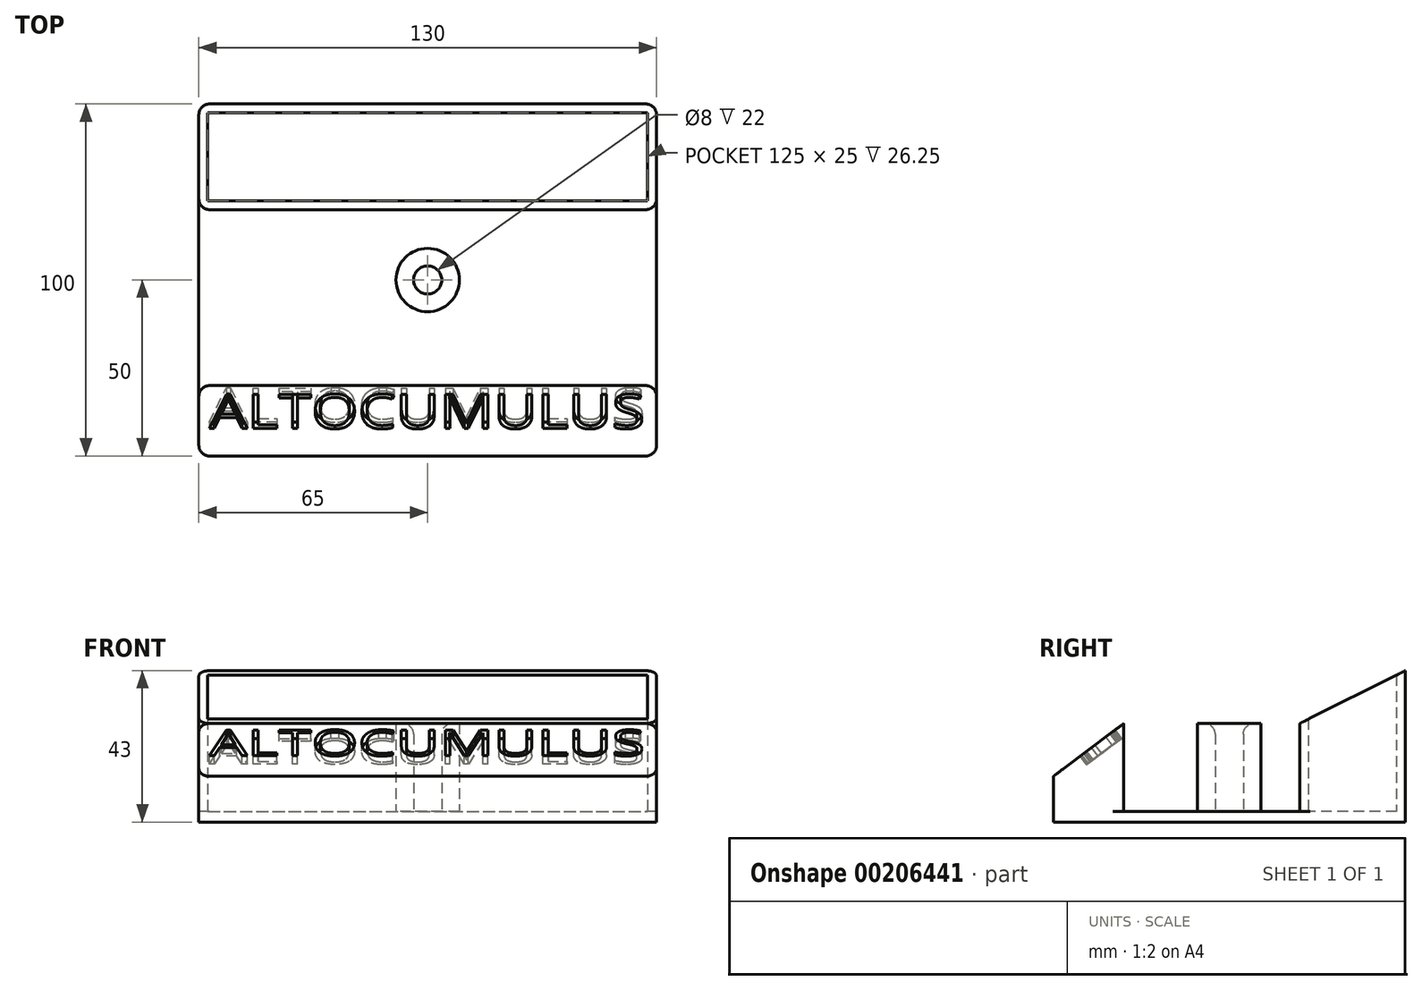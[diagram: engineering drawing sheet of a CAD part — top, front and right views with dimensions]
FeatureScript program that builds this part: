
annotation { "Feature Type Name" : "Feature", "Feature Type Description" : "" }
export const myFeature = defineFeature(function(context is Context, id is Id, definition is map)
    precondition{}
    {
        {
            var Q0;
            Q0=qCreatedBy(makeId("Top.planeOp"),FACE);
            var sketch = newSketch(context, id + "F0", { "sketchPlane" : qUnion([Q0])});
            skLineSegment(sketch, "E0.bottom", {"start": v(-65, 100) * mm, "end": v(65, 100) * mm});
            skLineSegment(sketch, "E0.top", {"start": v(-65, 0) * mm, "end": v(65, 0) * mm});
            skLineSegment(sketch, "E0.left", {"start": v(65, 100) * mm, "end": v(65, 0) * mm});
            skLineSegment(sketch, "E0.right", {"start": v(-65, 100) * mm, "end": v(-65, 0) * mm});
            skSolve(sketch);
        }
        {
            var Q0;
            Q0=makeQuery(id+"F0.imprint","IMPRINT",FACE,{"disambiguationData":[TD([[makeQuery(id+"F0.imprint","IMPRINT",EDGE,{"derivedFrom":sQuery(id+"F0.wireOp",EDGE,"E0.bottom")}),-1.0]])]});
            extrude(context, id + "F1", {"entities" : qUnion([Q0]), "depth" : 3 * mm});
        }
        {
            var Q0;
            Q0=makeQuery(id+"F1.opExtrude","CAP_FACE",FACE,{"disambiguationData":[OSD([sQuery(id+"F0.wireOp",EDGE,"E0.bottom"),sQuery(id+"F0.wireOp",EDGE,"E0.top"),sQuery(id+"F0.wireOp",EDGE,"E0.left"),sQuery(id+"F0.wireOp",EDGE,"E0.right")])],"isStart":false});
            var sketch = newSketch(context, id + "F2", { "sketchPlane" : qUnion([Q0])});
            skLineSegment(sketch, "E1", {"start": v(0, 0) * mm, "end": v(0, 100) * mm, "construction": true});
            skCircle(sketch, "E2", {"center": v(0, 50) * mm, "radius": 9 * mm});
            skCircle(sketch, "E3", {"center": v(0, 50) * mm, "radius": 4 * mm});
            skLineSegment(sketch, "E4.bottom", {"start": v(-65, 0) * mm, "end": v(65, 0) * mm});
            skLineSegment(sketch, "E4.top", {"start": v(-65, 20) * mm, "end": v(65, 20) * mm});
            skLineSegment(sketch, "E4.left", {"start": v(-65, 0) * mm, "end": v(-65, 20) * mm});
            skLineSegment(sketch, "E4.right", {"start": v(65, 0) * mm, "end": v(65, 20) * mm});
            skLineSegment(sketch, "E5.bottom", {"start": v(-65, 100) * mm, "end": v(65, 100) * mm});
            skLineSegment(sketch, "E5.top", {"start": v(-65, 70) * mm, "end": v(65, 70) * mm});
            skLineSegment(sketch, "E5.left", {"start": v(-65, 100) * mm, "end": v(-65, 70) * mm});
            skLineSegment(sketch, "E5.right", {"start": v(65, 100) * mm, "end": v(65, 70) * mm});
            skLineSegment(sketch, "E6.0", {"start": v(62.5, 97.5) * mm, "end": v(62.5, 72.5) * mm});
            skLineSegment(sketch, "E6.1", {"start": v(-62.5, 97.5) * mm, "end": v(62.5, 97.5) * mm});
            skLineSegment(sketch, "E6.2", {"start": v(-62.5, 97.5) * mm, "end": v(-62.5, 72.5) * mm});
            skLineSegment(sketch, "E6.3", {"start": v(-62.5, 72.5) * mm, "end": v(62.5, 72.5) * mm});
            skSolve(sketch);
        }
        {
            var Q0;
            Q0=makeQuery(id+"F2.imprint","IMPRINT",FACE,{"disambiguationData":[TD([[makeQuery(id+"F2.imprint","IMPRINT",EDGE,{"derivedFrom":sQuery(id+"F2.wireOp",EDGE,"E5.bottom")}),-1.0]])]});
            extrude(context, id + "F3", {"entities" : qUnion([Q0]), "operationType" : NewBodyOperationType.ADD, "depth" : 40 * mm});
        }
        {
            var Q0;
            Q0=makeQuery(id+"F2.imprint","IMPRINT",FACE,{"disambiguationData":[TD([[makeQuery(id+"F2.imprint","IMPRINT",EDGE,{"derivedFrom":sQuery(id+"F2.wireOp",EDGE,"E2")}),1.0]])]});
            var Q1;
            Q1=makeQuery(id+"F2.imprint","IMPRINT",FACE,{"disambiguationData":[TD([[makeQuery(id+"F2.imprint","IMPRINT",EDGE,{"derivedFrom":sQuery(id+"F2.wireOp",EDGE,"E4.bottom")}),1.0]])]});
            extrude(context, id + "F4", {"entities" : qUnion([Q0, Q1]), "operationType" : NewBodyOperationType.ADD, "depth" : 25 * mm});
        }
        {
            var Q0;
            Q0=makeQuery(id+"F4.opExtrude","CAP_EDGE",EDGE,{"disambiguationData":[OSD([sQuery(id+"F2.wireOp",EDGE,"E4.bottom")])],"isStart":false});
            chamfer(context, id + "F5", {"entities" : qUnion([Q0]), "chamferType" : ChamferType.TWO_OFFSETS, "width1" : 20 * mm, "oppositeDirection" : false, "width2" : 15 * mm, "tangentPropagation" : true});
        }
        {
            var Q0;
            Q0=makeQuery(id+"F3.opExtrude","CAP_EDGE",EDGE,{"disambiguationData":[OSD([sQuery(id+"F2.wireOp",EDGE,"E5.top")])],"isStart":false});
            chamfer(context, id + "F6", {"entities" : qUnion([Q0]), "chamferType" : ChamferType.TWO_OFFSETS, "width1" : 30 * mm, "oppositeDirection" : false, "width2" : 15 * mm, "tangentPropagation" : true});
        }
        {
            var Q0;
            Q0=makeQuery(id+"F3.boolean.opBoolean","MERGE",EDGE,{"derivedFrom":[makeQuery(id+"F1.opExtrude","SWEPT_EDGE",EDGE,{"disambiguationData":[OSD([sQuery(id+"F0.wireOp",EDGE,"E0.bottom"),sQuery(id+"F0.wireOp",EDGE,"E0.right")])]}),makeQuery(id+"F3.opExtrude","SWEPT_EDGE",EDGE,{"disambiguationData":[OSD([sQuery(id+"F2.wireOp",EDGE,"E5.bottom"),sQuery(id+"F2.wireOp",EDGE,"E5.left")])]})]});
            var Q1;
            Q1=makeQuery(id+"F3.opExtrude","SWEPT_EDGE",EDGE,{"disambiguationData":[OSD([sQuery(id+"F0.wireOp",EDGE,"E0.right"),sQuery(id+"F2.wireOp",EDGE,"E5.top"),sQuery(id+"F2.wireOp",EDGE,"E5.left")])]});
            var Q2;
            Q2=makeQuery(id+"F3.opExtrude","SWEPT_EDGE",EDGE,{"disambiguationData":[OSD([sQuery(id+"F0.wireOp",EDGE,"E0.left"),sQuery(id+"F2.wireOp",EDGE,"E5.top"),sQuery(id+"F2.wireOp",EDGE,"E5.right")])]});
            var Q3;
            Q3=makeQuery(id+"F4.boolean.opBoolean","MERGE",EDGE,{"derivedFrom":[makeQuery(id+"F1.opExtrude","SWEPT_EDGE",EDGE,{"disambiguationData":[OSD([sQuery(id+"F0.wireOp",EDGE,"E0.top"),sQuery(id+"F0.wireOp",EDGE,"E0.right")])]}),makeQuery(id+"F4.opExtrude","SWEPT_EDGE",EDGE,{"disambiguationData":[OSD([sQuery(id+"F2.wireOp",EDGE,"E4.bottom"),sQuery(id+"F2.wireOp",EDGE,"E4.left")])]})]});
            var Q4;
            Q4=makeQuery(id+"F3.boolean.opBoolean","MERGE",EDGE,{"derivedFrom":[makeQuery(id+"F1.opExtrude","SWEPT_EDGE",EDGE,{"disambiguationData":[OSD([sQuery(id+"F0.wireOp",EDGE,"E0.bottom"),sQuery(id+"F0.wireOp",EDGE,"E0.left")])]}),makeQuery(id+"F3.opExtrude","SWEPT_EDGE",EDGE,{"disambiguationData":[OSD([sQuery(id+"F2.wireOp",EDGE,"E5.bottom"),sQuery(id+"F2.wireOp",EDGE,"E5.right")])]})]});
            var Q5;
            Q5=makeQuery(id+"F4.boolean.opBoolean","MERGE",EDGE,{"derivedFrom":[makeQuery(id+"F1.opExtrude","SWEPT_EDGE",EDGE,{"disambiguationData":[OSD([sQuery(id+"F0.wireOp",EDGE,"E0.top"),sQuery(id+"F0.wireOp",EDGE,"E0.left")])]}),makeQuery(id+"F4.opExtrude","SWEPT_EDGE",EDGE,{"disambiguationData":[OSD([sQuery(id+"F2.wireOp",EDGE,"E4.bottom"),sQuery(id+"F2.wireOp",EDGE,"E4.right")])]})]});
            var Q6;
            Q6=makeQuery(id+"F4.opExtrude","SWEPT_EDGE",EDGE,{"disambiguationData":[OSD([sQuery(id+"F0.wireOp",EDGE,"E0.left"),sQuery(id+"F2.wireOp",EDGE,"E4.top"),sQuery(id+"F2.wireOp",EDGE,"E4.right")])]});
            var Q7;
            Q7=makeQuery(id+"F4.opExtrude","SWEPT_EDGE",EDGE,{"disambiguationData":[OSD([sQuery(id+"F0.wireOp",EDGE,"E0.right"),sQuery(id+"F2.wireOp",EDGE,"E4.top"),sQuery(id+"F2.wireOp",EDGE,"E4.left")])]});
            var Q8;
            Q8=makeQuery(id+"F4.opExtrude","CAP_EDGE",EDGE,{"disambiguationData":[OSD([sQuery(id+"F2.wireOp",EDGE,"E3")])],"isStart":false});
            fillet(context, id + "F7", {"entities" : qUnion([Q0, Q1, Q2, Q3, Q4, Q5, Q6, Q7, Q8]), "radius" : 3 * mm, "tangentPropagation" : true, "allowEdgeOverflow" : false});
        }
        {
            var Q0;
            Q0=makeQuery(id+"F5.opChamfer","BLEND_FACE",FACE,{"disambiguationData":[OSD([sQuery(id+"F2.wireOp",EDGE,"E4.bottom")])]});
            var sketch = newSketch(context, id + "F8", { "sketchPlane" : qUnion([Q0])});
            skLineSegment(sketch, "E7.0", {"start": v(62, 10.8) * mm, "end": v(-62, 10.8) * mm});
            skLineSegment(sketch, "E8.0", {"start": v(-62, 29.8) * mm, "end": v(62, 29.8) * mm});
            skText(sketch, "E9", { "text": "ALTOCUMULUS", "fontName": "OpenSans-Regular.ttf"});
            const initialGuessF8  = {"E9": [-0.062, 0.01755, 1, 0, 0.01225]};
            skSetInitialGuess(sketch, initialGuessF8);
            skSolve(sketch);
        }
        {
            var Q0;
            Q0=makeQuery(id+"F8.imprint","IMPRINT",FACE,{"disambiguationData":[TD([[makeQuery(id+"F8.imprint","IMPRINT",EDGE,{"derivedFrom":sQuery(id+"F8.wireOp",EDGE,"E9.sketch_text.stroke-0")}),-1.0]])]});
            var Q1;
            Q1=makeQuery(id+"F8.imprint","IMPRINT",FACE,{"disambiguationData":[TD([[makeQuery(id+"F8.imprint","IMPRINT",EDGE,{"derivedFrom":sQuery(id+"F8.wireOp",EDGE,"E9.sketch_text.stroke-13")}),-1.0]])]});
            var Q2;
            Q2=makeQuery(id+"F8.imprint","IMPRINT",FACE,{"disambiguationData":[TD([[makeQuery(id+"F8.imprint","IMPRINT",EDGE,{"derivedFrom":sQuery(id+"F8.wireOp",EDGE,"E9.sketch_text.stroke-19")}),-1.0]])]});
            var Q3;
            Q3=makeQuery(id+"F8.imprint","IMPRINT",FACE,{"disambiguationData":[TD([[makeQuery(id+"F8.imprint","IMPRINT",EDGE,{"derivedFrom":sQuery(id+"F8.wireOp",EDGE,"E9.sketch_text.stroke-27")}),-1.0]])]});
            var Q4;
            Q4=makeQuery(id+"F8.imprint","IMPRINT",FACE,{"disambiguationData":[TD([[makeQuery(id+"F8.imprint","IMPRINT",EDGE,{"derivedFrom":sQuery(id+"F8.wireOp",EDGE,"E9.sketch_text.stroke-43")}),-1.0]])]});
            var Q5;
            Q5=makeQuery(id+"F8.imprint","IMPRINT",FACE,{"disambiguationData":[TD([[makeQuery(id+"F8.imprint","IMPRINT",EDGE,{"derivedFrom":sQuery(id+"F8.wireOp",EDGE,"E9.sketch_text.stroke-58")}),-1.0]])]});
            var Q6;
            Q6=makeQuery(id+"F8.imprint","IMPRINT",FACE,{"disambiguationData":[TD([[makeQuery(id+"F8.imprint","IMPRINT",EDGE,{"derivedFrom":sQuery(id+"F8.wireOp",EDGE,"E9.sketch_text.stroke-72")}),-1.0]])]});
            var Q7;
            Q7=makeQuery(id+"F8.imprint","IMPRINT",FACE,{"disambiguationData":[TD([[makeQuery(id+"F8.imprint","IMPRINT",EDGE,{"derivedFrom":sQuery(id+"F8.wireOp",EDGE,"E9.sketch_text.stroke-90")}),-1.0]])]});
            var Q8;
            Q8=makeQuery(id+"F8.imprint","IMPRINT",FACE,{"disambiguationData":[TD([[makeQuery(id+"F8.imprint","IMPRINT",EDGE,{"derivedFrom":sQuery(id+"F8.wireOp",EDGE,"E9.sketch_text.stroke-104")}),-1.0]])]});
            var Q9;
            Q9=makeQuery(id+"F8.imprint","IMPRINT",FACE,{"disambiguationData":[TD([[makeQuery(id+"F8.imprint","IMPRINT",EDGE,{"derivedFrom":sQuery(id+"F8.wireOp",EDGE,"E9.sketch_text.stroke-110")}),-1.0]])]});
            var Q10;
            Q10=makeQuery(id+"F8.imprint","IMPRINT",FACE,{"disambiguationData":[TD([[makeQuery(id+"F8.imprint","IMPRINT",EDGE,{"derivedFrom":sQuery(id+"F8.wireOp",EDGE,"E9.sketch_text.stroke-124")}),-1.0]])]});
            extrude(context, id + "F9", {"entities" : qUnion([Q0, Q1, Q2, Q3, Q4, Q5, Q6, Q7, Q8, Q9, Q10]), "operationType" : NewBodyOperationType.REMOVE, "oppositeDirection" : true, "depth" : 3 * mm});
        }
    });
